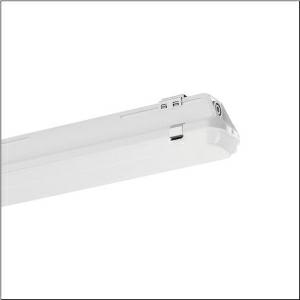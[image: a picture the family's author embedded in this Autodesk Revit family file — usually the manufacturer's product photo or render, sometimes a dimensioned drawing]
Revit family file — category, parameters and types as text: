
# Revit family: monsun_r__21_emergency_51fb10dp468c2_3e12
name_source: partatom
category: Lighting Fixtures
units: mm (PartAtom-declared; Revit-internal decimal feet)

## family parameters
Cut with Voids When Loaded = No
Host = Face
Light Source = No
Part Type = Normal
Room Calculation Point = No
Round Connector Dimension = Use Diameter
Shared = No

## types (1)
- --- (1 x LED, 930 lm, 6.2 W, 4000K)
    Apparent Load = 6 VA
    CIE Flux Codes = 47 77 93 94 100
    Color Rendering = 80
    Color Temperature = 4000K
    Default Elevation = 1800 mm
    Description = Monsun® 21 emergency, damp-proof luminaire, chain hanger, primary optical cover: enclosure, of PMMA, light emission: direct distribution, primary light characteristic: symmetric, installation type: suspended mounting, surface-mounted, horizontal mounting, vertical mounting, LED, rated luminous flux: 6.060lm, luminous efficacy: 185lm/W, light colour: 840, colour temperature: 4000K, control gear: DALI 2, with terminal, 5-pole, max. 2.5mm², mains connection: 220..240V, AC/DC, 0/50..60Hz, rated input power: 33W, housing, of glass-fibre reinforced polyester, uncoated, bright grey, incl. chain hanger, length: 1.590mm, width: 90mm, height: 88mm, clip for enclosure, of stainless steel (V2A), ceiling mounting element, of stainless steel (V2A), chain hanger, of stainless steel (V2A), protection rating (complete): IP66, insulation class (complete): insulation class I (protective earthing), certification: CE, UKCA, protection symbol: D, impact resistance: IK04, permissible operating ambient temperature: -25..+35°C, standard: EN 50419, EN 60598-2-1, EN 60598-2-22, corresponds to IFS (International Featured Standards) requirements for safety and quality in the food industry, for indoor or canopied outdoor use, no direct snow, no direct sun, no direct rain, LABS conformity tested according to VDMA 24364:2018-05, contact your sales advisor before using the luminaires in applications with unclear chemical exposure, large temperature fluctuations or condensation-forming humidity, packaging unit: 1 piece
    Height = 89 mm
    Lamp = 1 x LED
    Lamp Light Flux = 930 lm
    Lamp Power = 6.2 W
    Lamp count = 1
    Length = 1590 mm
    Luminous efficacy = 150 lm/W
    Manufacturer = Siteco
    ModVariant = No
    Model = 51FB10DP468C2
    Mounting Place = Ceiling
    Mounting Type = Surface mounted
    Number of Poles = 1
    OnlyDefault = Yes
    Power Factor = 1
    Product Name = Monsun® 21 emergency
    Product group = damp-proof luminaire
    ProductGroupID = 301
    Protection Class = Protection class I
    Protection Degree = IP 66
    RLX_Detail_Level = 1
    RLX_Emergency_Light_Flux = 0 lm
    RLX_Emergency_Type = 0
    RLX_Emergency_Type_DB = No
    RlxData = <blob elided: 92525 chars, md5=1c079ba9>
    Socket = socket
    Standby Power = 0 W
    System Light Flux = 930 lm
    System Power = 6 W
    Type Comments = : equivalent power supply (DC)
    Type Image = l_1319656.jpg
    URL = http://relux.com
    VarID = @adj_051723
    Voltage = 0 V
    Weight = 0.00 kg
    Width = 90 mm

## geometry (parser evidence)
native form markers: Blend x4, Sweep x13
no freeform markers — native parametric forms only
